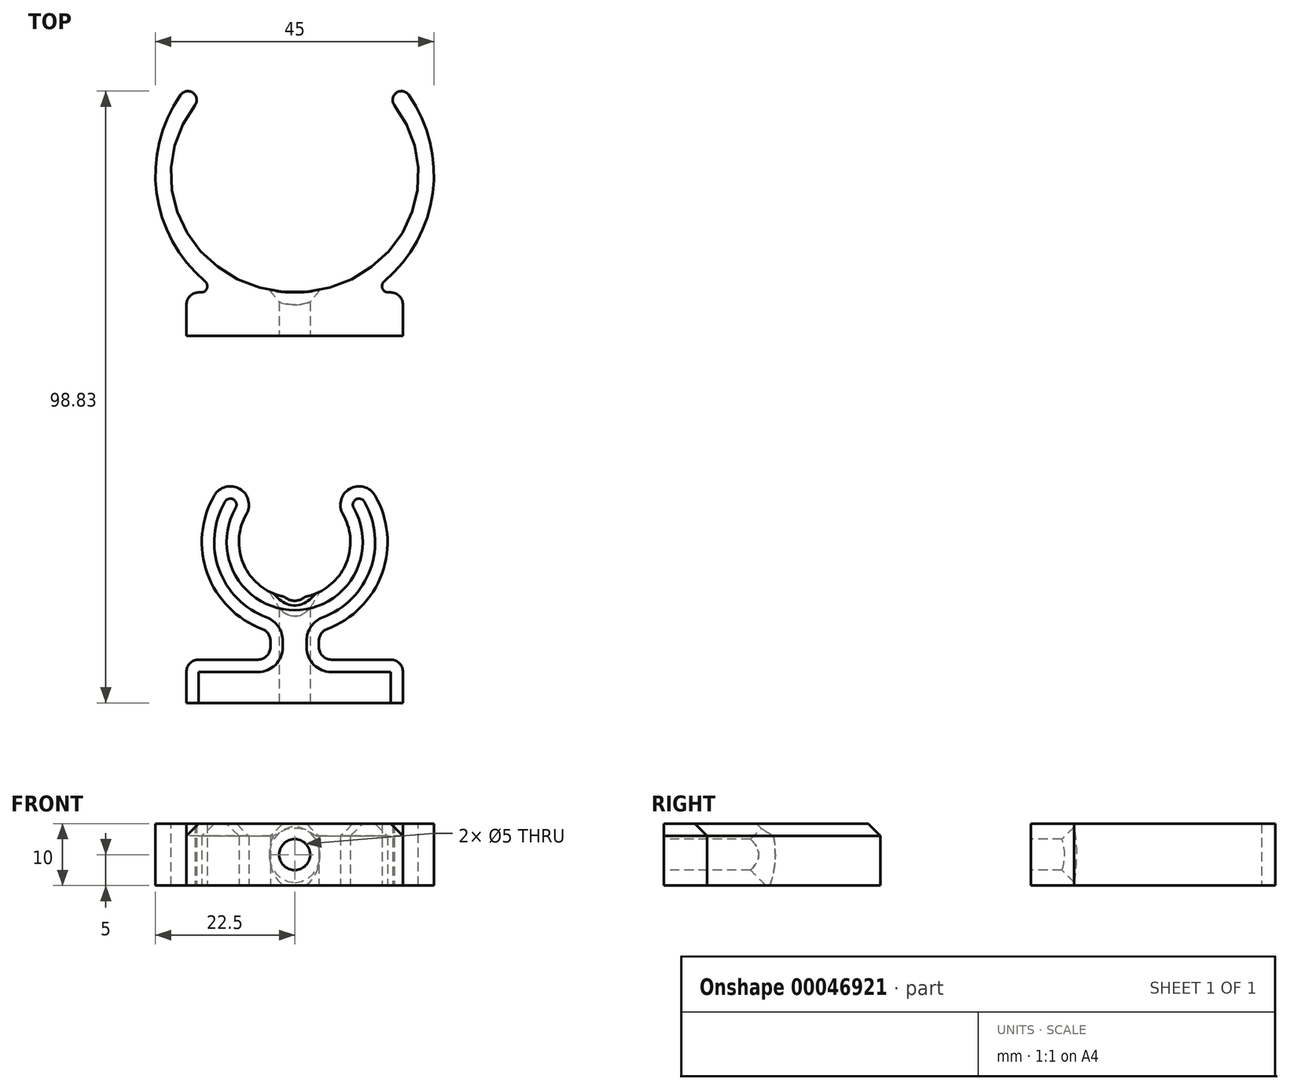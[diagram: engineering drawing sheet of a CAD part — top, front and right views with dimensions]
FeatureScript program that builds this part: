
annotation { "Feature Type Name" : "Feature", "Feature Type Description" : "" }
export const myFeature = defineFeature(function(context is Context, id is Id, definition is map)
    precondition{}
    {
        {
            var Q0;
            Q0=qCreatedBy(makeId("Top.planeOp"),FACE);
            var sketch = newSketch(context, id + "F0", { "sketchPlane" : qUnion([Q0])});
            skArc(sketch, "E0", {"start": v(-18.43, 12.9) * mm, "mid": v(-22.3, -2.94) * mm, "end": v(-14.47, -17.23) * mm});
            skEllipticalArc(sketch, "E1", {});
            skCircle(sketch, "E2", {"center": v(0, 0) * mm, "radius": 19 * mm, "construction": true});
            skLineSegment(sketch, "E3", {"start": v(0, 0) * mm, "end": v(-24.83, 17.38) * mm, "construction": true});
            skLineSegment(sketch, "E4", {"start": v(-18.43, 12.9) * mm, "end": v(-16.1, 11.27) * mm, "construction": true});
            skArc(sketch, "E5", {"start": v(-16.1, 11.27) * mm, "mid": v(-16.45, 13.25) * mm, "end": v(-18.43, 12.9) * mm});
            skArc(sketch, "E6.MirrorC", {"start": v(16.1, 11.27) * mm, "mid": v(16.45, 13.25) * mm, "end": v(18.43, 12.9) * mm});
            skLineSegment(sketch, "E7.MirrorCS", {"start": v(0, 0) * mm, "end": v(24.83, 17.38) * mm, "construction": true});
            skLineSegment(sketch, "E8.rect.bottom", {"start": v(15.5, -19) * mm, "end": v(15.1, -19) * mm});
            skLineSegment(sketch, "E8.rect.top", {"start": v(17.5, -26) * mm, "end": v(-17.5, -26) * mm});
            skLineSegment(sketch, "E8.rect.left", {"start": v(17.5, -21) * mm, "end": v(17.5, -26) * mm});
            skLineSegment(sketch, "E8.rect.right", {"start": v(-17.5, -21) * mm, "end": v(-17.5, -26) * mm});
            skPoint(sketch, "E8.rect.middle", {"position": v(0, -22.5) * mm});
            skArc(sketch, "E9.trimOffspring", {"start": v(14.47, -17.23) * mm, "mid": v(22.3, -2.94) * mm, "end": v(18.43, 12.9) * mm});
            skLineSegment(sketch, "E10.trimOffspring", {"start": v(-15.1, -19) * mm, "end": v(-15.5, -19) * mm});
            skPoint(sketch, "E11.visualSharp", {"position": v(-12.05, -19) * mm});
            skArc(sketch, "E11.filletArc", {"start": v(-15.1, -19) * mm, "mid": v(-14.17, -18.34) * mm, "end": v(-14.47, -17.23) * mm});
            skPoint(sketch, "E12.visualSharp", {"position": v(12.05, -19) * mm});
            skArc(sketch, "E12.filletArc", {"start": v(14.47, -17.23) * mm, "mid": v(14.17, -18.34) * mm, "end": v(15.1, -19) * mm});
            skPoint(sketch, "E13.visualSharp", {"position": v(-17.5, -19) * mm});
            skArc(sketch, "E13.filletArc", {"start": v(-15.5, -19) * mm, "mid": v(-16.91, -19.59) * mm, "end": v(-17.5, -21) * mm});
            skPoint(sketch, "E14.visualSharp", {"position": v(17.5, -19) * mm});
            skArc(sketch, "E14.filletArc", {"start": v(17.5, -21) * mm, "mid": v(16.91, -19.59) * mm, "end": v(15.5, -19) * mm});
            const initialGuessF0  = {"E1": [0, 0, 1, 0, 0.02, 0.019, 2.5064243449638544, 1.5707963267948966]};
            skSetInitialGuess(sketch, initialGuessF0);
            skSolve(sketch);
        }
        {
            var Q0;
            Q0=makeQuery(id+"F0.imprint","IMPRINT",FACE,{"disambiguationData":[TD([[makeQuery(id+"F0.imprint","IMPRINT",EDGE,{"derivedFrom":sQuery(id+"F0.wireOp",EDGE,"E0")}),1.0]])]});
            extrude(context, id + "F1", {"entities" : qUnion([Q0]), "depth" : 10 * mm});
        }
        {
            var Q0;
            Q0=makeQuery(id+"F1.opExtrude","SWEPT_FACE",FACE,{"disambiguationData":[OSD([sQuery(id+"F0.wireOp",EDGE,"E8.rect.top")])]});
            var sketch = newSketch(context, id + "F2", { "sketchPlane" : qUnion([Q0])});
            skLineSegment(sketch, "E15", {"start": v(0, 10) * mm, "end": v(0, 0) * mm, "construction": true});
            skCircle(sketch, "E16", {"center": v(0, 5) * mm, "radius": 2.5 * mm});
            skSolve(sketch);
        }
        {
            var Q0;
            Q0=makeQuery(id+"F2.imprint","IMPRINT",FACE,{"disambiguationData":[TD([[makeQuery(id+"F2.imprint","IMPRINT",EDGE,{"derivedFrom":sQuery(id+"F2.wireOp",EDGE,"E16")}),1.0]])]});
            extrude(context, id + "F3", {"entities" : qUnion([Q0]), "operationType" : NewBodyOperationType.REMOVE, "endBound" : BoundingType.THROUGH_ALL, "oppositeDirection" : true, "depth" : 25 * mm});
        }
        {
            var Q0;
            Q0=makeQuery(id+"F3.boolean.opBoolean","INTERSECT",EDGE,{"derivedFrom":[makeQuery(id+"F1.opExtrude","SWEPT_FACE",FACE,{"disambiguationData":[OSD([sQuery(id+"F0.wireOp",EDGE,"E1")])]}),makeQuery(id+"F3.opExtrude","SWEPT_FACE",FACE,{"disambiguationData":[OSD([sQuery(id+"F2.wireOp",EDGE,"E16")])]})]});
            chamfer(context, id + "F4", {"entities" : qUnion([Q0]), "width" : 2 * mm, "tangentPropagation" : true});
        }
        {
            var Q0;
            Q0=qCreatedBy(makeId("Top.planeOp"),FACE);
            var sketch = newSketch(context, id + "F5", { "sketchPlane" : qUnion([Q0])});
            skLineSegment(sketch, "E17", {"start": v(-25.4, -59.32) * mm, "end": v(30.6, -59.32) * mm, "construction": true});
            skArc(sketch, "E18", {"start": v(-7.8, -54.82) * mm, "mid": v(0, -68.32) * mm, "end": v(7.8, -54.82) * mm});
            skArc(sketch, "E19", {"start": v(5.23, -73.38) * mm, "mid": v(14.11, -64.4) * mm, "end": v(13, -51.82) * mm});
            skPoint(sketch, "E20.rect.middle", {"position": v(0, -74.32) * mm});
            skLineSegment(sketch, "E21.rect.bottom", {"start": v(15.5, -78.32) * mm, "end": v(5.92, -78.32) * mm});
            skLineSegment(sketch, "E21.rect.top", {"start": v(17.5, -85.32) * mm, "end": v(-17.5, -85.32) * mm});
            skLineSegment(sketch, "E21.rect.left", {"start": v(17.5, -80.32) * mm, "end": v(17.5, -85.32) * mm});
            skLineSegment(sketch, "E21.rect.right", {"start": v(-17.5, -80.32) * mm, "end": v(-17.5, -85.32) * mm});
            skPoint(sketch, "E21.rect.middle", {"position": v(0, -81.82) * mm});
            skLineSegment(sketch, "E22.rect.left", {"start": v(3.92, -75.25) * mm, "end": v(3.92, -76.32) * mm});
            skLineSegment(sketch, "E22.rect.right", {"start": v(-3.92, -75.25) * mm, "end": v(-3.92, -76.32) * mm});
            skPoint(sketch, "E23.orphan", {"position": v(-3.92, -69.66) * mm});
            skPoint(sketch, "E24.orphan", {"position": v(3.92, -67.07) * mm});
            skPoint(sketch, "E25.orphan", {"position": v(3.92, -78.98) * mm});
            skPoint(sketch, "E26.orphan", {"position": v(-3.92, -81.57) * mm});
            skLineSegment(sketch, "E27.trimOffspring", {"start": v(-5.92, -78.32) * mm, "end": v(-15.5, -78.32) * mm});
            skPoint(sketch, "E28.visualSharp", {"position": v(-3.92, -73.8) * mm});
            skArc(sketch, "E28.filletArc", {"start": v(-3.92, -75.25) * mm, "mid": v(-4.28, -74.11) * mm, "end": v(-5.23, -73.38) * mm});
            skPoint(sketch, "E29.visualSharp", {"position": v(3.92, -73.8) * mm});
            skArc(sketch, "E29.filletArc", {"start": v(5.23, -73.38) * mm, "mid": v(4.28, -74.11) * mm, "end": v(3.92, -75.25) * mm});
            skPoint(sketch, "E30.visualSharp", {"position": v(3.92, -78.32) * mm});
            skArc(sketch, "E30.filletArc", {"start": v(3.92, -76.32) * mm, "mid": v(4.5, -77.73) * mm, "end": v(5.92, -78.32) * mm});
            skPoint(sketch, "E31.visualSharp", {"position": v(-3.92, -78.32) * mm});
            skArc(sketch, "E31.filletArc", {"start": v(-5.92, -78.32) * mm, "mid": v(-4.5, -77.73) * mm, "end": v(-3.92, -76.32) * mm});
            skPoint(sketch, "E32.visualSharp", {"position": v(-17.5, -78.32) * mm});
            skArc(sketch, "E32.filletArc", {"start": v(-15.5, -78.32) * mm, "mid": v(-16.91, -78.9) * mm, "end": v(-17.5, -80.32) * mm});
            skPoint(sketch, "E33.visualSharp", {"position": v(17.5, -78.32) * mm});
            skArc(sketch, "E33.filletArc", {"start": v(17.5, -80.32) * mm, "mid": v(16.91, -78.9) * mm, "end": v(15.5, -78.32) * mm});
            skLineSegment(sketch, "E34", {"start": v(0, -59.32) * mm, "end": v(-19.58, -48.02) * mm, "construction": true});
            skLineSegment(sketch, "E35.MirrorCS", {"start": v(0, -59.32) * mm, "end": v(19.58, -48.02) * mm, "construction": true});
            skLineSegment(sketch, "E36", {"start": v(-7.8, -54.82) * mm, "end": v(-13, -51.82) * mm, "construction": true});
            skArc(sketch, "E37", {"start": v(-7.8, -54.82) * mm, "mid": v(-8.9, -50.72) * mm, "end": v(-13, -51.82) * mm});
            skArc(sketch, "E38.MirrorCS", {"start": v(7.8, -54.82) * mm, "mid": v(8.9, -50.72) * mm, "end": v(13, -51.82) * mm});
            skArc(sketch, "E39.trimOffspring", {"start": v(-13, -51.82) * mm, "mid": v(-14.11, -64.4) * mm, "end": v(-5.23, -73.38) * mm});
            skPoint(sketch, "E40.rect.middle", {"position": v(0, -51.04) * mm});
            skSolve(sketch);
        }
        {
            var Q0;
            Q0=makeQuery(id+"F5.imprint","IMPRINT",FACE,{"disambiguationData":[TD([[makeQuery(id+"F5.imprint","IMPRINT",EDGE,{"derivedFrom":sQuery(id+"F5.wireOp",EDGE,"E18")}),-1.0]])]});
            extrude(context, id + "F6", {"entities" : qUnion([Q0]), "depth" : 10 * mm});
        }
        {
            var Q0;
            Q0=makeQuery(id+"F6.opExtrude","CAP_EDGE",EDGE,{"disambiguationData":[OSD([sQuery(id+"F5.wireOp",EDGE,"E18")])],"isStart":false});
            chamfer(context, id + "F7", {"entities" : qUnion([Q0]), "width" : 2 * mm, "tangentPropagation" : true});
        }
        {
            var Q0;
            Q0=makeQuery(id+"F6.opExtrude","SWEPT_FACE",FACE,{"disambiguationData":[OSD([sQuery(id+"F5.wireOp",EDGE,"E21.rect.top")])]});
            var sketch = newSketch(context, id + "F8", { "sketchPlane" : qUnion([Q0])});
            skLineSegment(sketch, "E41", {"start": v(0, 8) * mm, "end": v(0, 2) * mm, "construction": true});
            skCircle(sketch, "E42", {"center": v(0, 5) * mm, "radius": 2.5 * mm});
            skSolve(sketch);
        }
        {
            var Q0;
            Q0=makeQuery(id+"F8.imprint","IMPRINT",FACE,{"disambiguationData":[TD([[makeQuery(id+"F8.imprint","IMPRINT",EDGE,{"derivedFrom":sQuery(id+"F8.wireOp",EDGE,"E42")}),1.0]])]});
            extrude(context, id + "F9", {"entities" : qUnion([Q0]), "operationType" : NewBodyOperationType.REMOVE, "oppositeDirection" : true, "depth" : 25 * mm});
        }
        {
            var Q0;
            Q0=makeQuery(id+"F9.boolean.opBoolean","INTERSECT",EDGE,{"derivedFrom":[makeQuery(id+"F6.opExtrude","SWEPT_FACE",FACE,{"disambiguationData":[OSD([sQuery(id+"F5.wireOp",EDGE,"E18")])]}),makeQuery(id+"F9.opExtrude","SWEPT_FACE",FACE,{"disambiguationData":[OSD([sQuery(id+"F8.wireOp",EDGE,"E42")])]})]});
            chamfer(context, id + "F10", {"entities" : qUnion([Q0]), "width" : 3 * mm, "tangentPropagation" : true});
        }
    });
